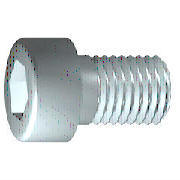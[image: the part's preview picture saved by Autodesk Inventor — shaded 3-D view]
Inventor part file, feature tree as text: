
AUTODESK INVENTOR PART (.ipt)
format: ipt  version: 2025 (Build 290162010, 162A)  size: 193,024 bytes
history: native  units: mm (DEFAULTED — no unit token found)
features: extrude x1, plane x1, fillet x1
ambient origin geometry x7: Origin, YZ Plane, XY Plane, X Axis, Y Axis, Z Axis, Center Point
bodies: Solid1 (feature_tree), Body (feature_tree)
feature tree (3):
  extrude  "Slot"  Depth=8.75mm
  plane  "Work Plane1"
  fillet  "Fillet2"  Radius=0.306825mm
